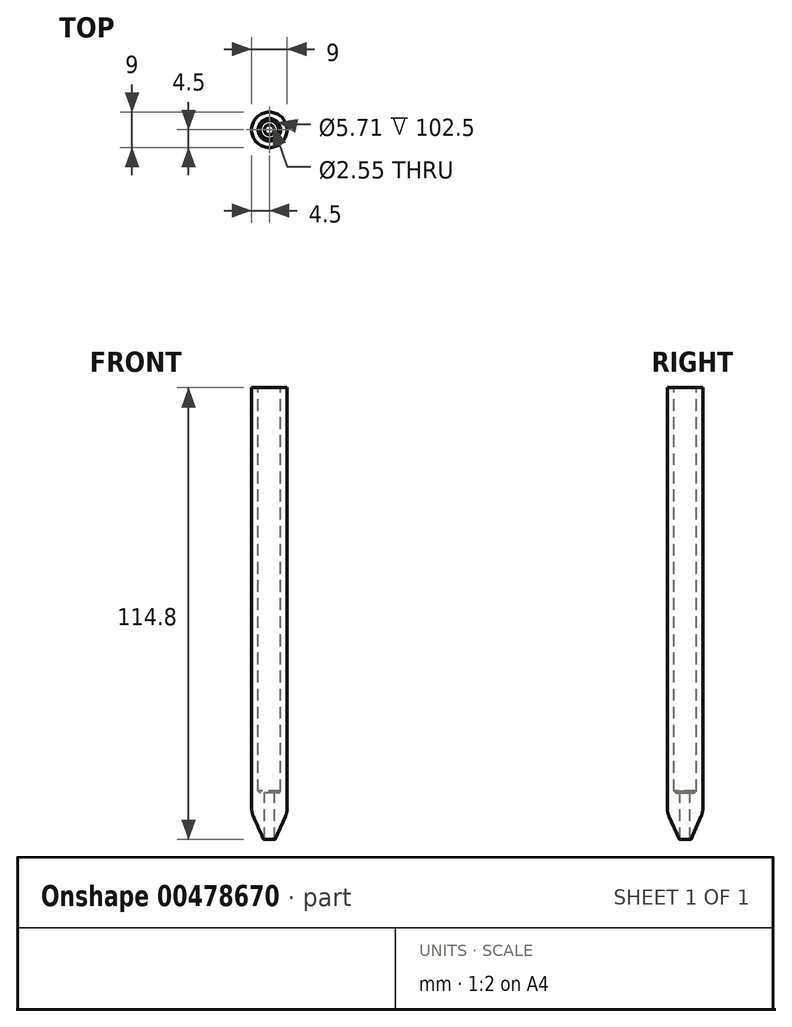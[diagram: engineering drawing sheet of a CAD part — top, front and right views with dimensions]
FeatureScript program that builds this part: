
annotation { "Feature Type Name" : "Feature", "Feature Type Description" : "" }
export const myFeature = defineFeature(function(context is Context, id is Id, definition is map)
    precondition{}
    {
        {
            var Q0;
            Q0=qCreatedBy(makeId("Front.planeOp"),FACE);
            var sketch = newSketch(context, id + "F0", { "sketchPlane" : qUnion([Q0])});
            skLineSegment(sketch, "E0", {"start": v(0, -37.5) * mm, "end": v(-4.5, -27.5) * mm});
            skLineSegment(sketch, "E1", {"start": v(-4.5, -27.5) * mm, "end": v(-4.5, 45.17) * mm});
            skLineSegment(sketch, "E2", {"start": v(-4.5, 45.17) * mm, "end": v(-4.5, 80.5) * mm});
            skLineSegment(sketch, "E3", {"start": v(-4.5, 80.5) * mm, "end": v(0, 80.5) * mm});
            skLineSegment(sketch, "E4", {"start": v(0, 80.5) * mm, "end": v(0, -37.5) * mm});
            skSolve(sketch);
        }
        {
            var Q0;
            Q0=makeQuery(id+"F0.imprint","IMPRINT",FACE,{"disambiguationData":[TD([[makeQuery(id+"F0.imprint","IMPRINT",EDGE,{"derivedFrom":sQuery(id+"F0.wireOp",EDGE,"E0")}),-1.0]])]});
            var Q1;
            Q1=sQuery(id+"F0.wireOp",EDGE,"E4");
            revolve(context, id + "F1", {"entities" : qUnion([Q0]), "axis" : qUnion([Q1]), "revolveType" : RevolveType.FULL});
        }
        {
            var Q0;
            Q0=makeQuery(id+"F1.opRevolve","SWEPT_FACE",FACE,{"disambiguationData":[OSD([sQuery(id+"F0.wireOp",EDGE,"E3")])]});
            var sketch = newSketch(context, id + "F2", { "sketchPlane" : qUnion([Q0])});
            skCircle(sketch, "E5", {"center": v(0, 0) * mm, "radius": 2.85 * mm});
            skSolve(sketch);
        }
        {
            var Q0;
            Q0=makeQuery(id+"F2.imprint","IMPRINT",FACE,{"disambiguationData":[TD([[makeQuery(id+"F2.imprint","IMPRINT",EDGE,{"derivedFrom":sQuery(id+"F2.wireOp",EDGE,"E5")}),1.0]])]});
            extrude(context, id + "F3", {"entities" : qUnion([Q0]), "operationType" : NewBodyOperationType.REMOVE, "oppositeDirection" : true, "depth" : 103 * mm});
        }
        {
            var Q0;
            Q0=makeQuery(id+"F3.boolean.opBoolean","COPY",FACE,{"derivedFrom":makeQuery(id+"F3.opExtrude","CAP_FACE",FACE,{"disambiguationData":[OSD([sQuery(id+"F2.wireOp",EDGE,"E5")])],"isStart":false})});
            var sketch = newSketch(context, id + "F4", { "sketchPlane" : qUnion([Q0])});
            skCircle(sketch, "E6", {"center": v(0, 0) * mm, "radius": 1.27 * mm});
            skSolve(sketch);
        }
        {
            var Q0;
            Q0 = qSketchRegion(id + "F4", true);
            extrude(context, id + "F5", {"entities" : qUnion([Q0]), "operationType" : NewBodyOperationType.REMOVE, "oppositeDirection" : true, "depth" : 25 * mm});
        }
        {
            var Q0;
            Q0=makeQuery(id+"F5.boolean.opBoolean","INTERSECT",EDGE,{"derivedFrom":[makeQuery(id+"F1.opRevolve","SWEPT_FACE",FACE,{"disambiguationData":[OSD([sQuery(id+"F0.wireOp",EDGE,"E0")])]}),makeQuery(id+"F5.opExtrude","SWEPT_FACE",FACE,{"disambiguationData":[OSD([sQuery(id+"F4.wireOp",EDGE,"E6")])]})]});
            fillet(context, id + "F6", {"entities" : qUnion([Q0]), "radius" : 0.1 * mm, "tangentPropagation" : true, "allowEdgeOverflow" : false});
        }
        {
            var Q0;
            Q0=makeQuery(id+"F3.boolean.opBoolean","COPY",EDGE,{"derivedFrom":makeQuery(id+"F3.opExtrude","CAP_EDGE",EDGE,{"disambiguationData":[OSD([sQuery(id+"F2.wireOp",EDGE,"E5")])],"isStart":false})});
            chamfer(context, id + "F7", {"entities" : qUnion([Q0]), "width" : 0.5 * mm, "tangentPropagation" : true});
        }
        {
            var Q0;
            Q0=makeQuery(id+"F1.opRevolve","SWEPT_EDGE",EDGE,{"disambiguationData":[OSD([sQuery(id+"F0.wireOp",EDGE,"E0"),sQuery(id+"F0.wireOp",EDGE,"E1")])]});
            fillet(context, id + "F8", {"entities" : qUnion([Q0]), "radius" : 5 * mm, "tangentPropagation" : true, "allowEdgeOverflow" : false});
        }
    });
